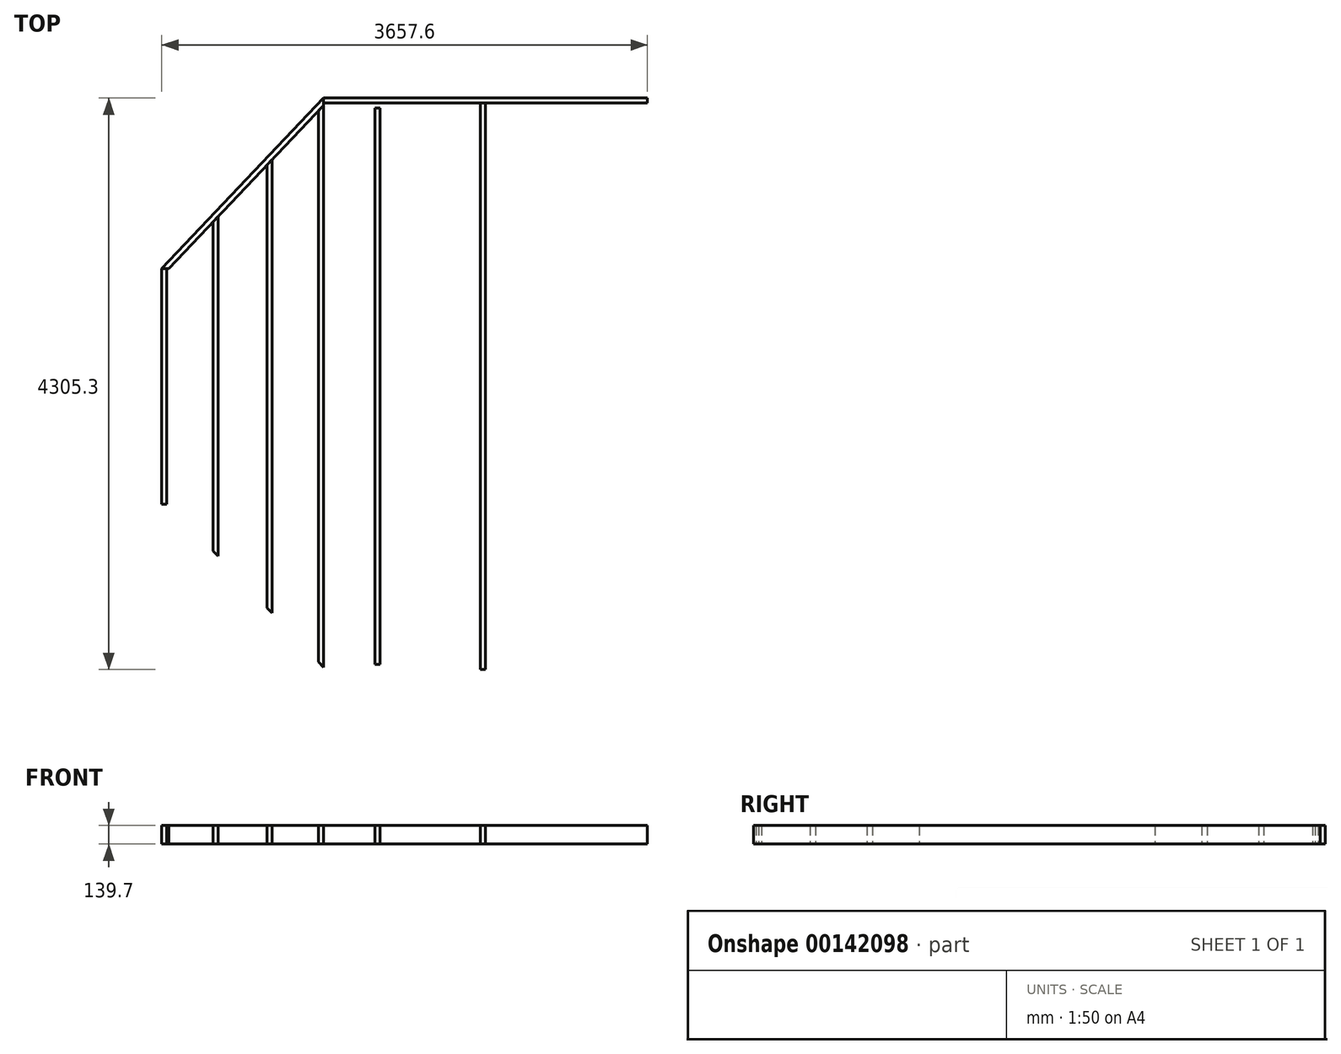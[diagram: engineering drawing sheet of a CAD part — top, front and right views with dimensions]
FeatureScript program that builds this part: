
annotation { "Feature Type Name" : "Feature", "Feature Type Description" : "" }
export const myFeature = defineFeature(function(context is Context, id is Id, definition is map)
    precondition{}
    {
        {
            var Q0;
            Q0=qCreatedBy(makeId("Top.planeOp"),FACE);
            var sketch = newSketch(context, id + "F0", { "sketchPlane" : qUnion([Q0])});
            skLineSegment(sketch, "E0", {"start": v(0, 0) * mm, "end": v(19.05, 0) * mm});
            skLineSegment(sketch, "E1.bottom", {"start": v(38.1, 2133.6) * mm, "end": v(0, 2133.6) * mm});
            skLineSegment(sketch, "E1.top", {"start": v(38.1, -2133.6) * mm, "end": v(0, -2133.6) * mm});
            skLineSegment(sketch, "E1.left", {"start": v(38.1, 2133.6) * mm, "end": v(38.1, -2133.6) * mm});
            skLineSegment(sketch, "E1.right", {"start": v(0, 2133.6) * mm, "end": v(0, -2133.6) * mm});
            skPoint(sketch, "E1.middle", {"position": v(19.05, 0) * mm});
            skLineSegment(sketch, "E2.bottom", {"start": v(38.1, 2133.6) * mm, "end": v(1181.1, 2133.6) * mm});
            skLineSegment(sketch, "E2.top", {"start": v(38.1, 2095.5) * mm, "end": v(1181.1, 2095.5) * mm});
            skLineSegment(sketch, "E2.left", {"start": v(38.1, 2133.6) * mm, "end": v(38.1, 2095.5) * mm});
            skLineSegment(sketch, "E2.right", {"start": v(1181.1, 2133.6) * mm, "end": v(1181.1, 2095.5) * mm});
            skLineSegment(sketch, "E3.bottom", {"start": v(1181.1, 2133.6) * mm, "end": v(1219.2, 2133.6) * mm});
            skLineSegment(sketch, "E3.top", {"start": v(1181.1, -2133.6) * mm, "end": v(1219.2, -2133.6) * mm});
            skLineSegment(sketch, "E3.left", {"start": v(1181.1, 2133.6) * mm, "end": v(1181.1, -2133.6) * mm});
            skLineSegment(sketch, "E3.right", {"start": v(1219.2, 2133.6) * mm, "end": v(1219.2, -2133.6) * mm});
            skLineSegment(sketch, "E4.MirrorCS", {"start": v(38.1, -2095.5) * mm, "end": v(1181.1, -2095.5) * mm});
            skLineSegment(sketch, "E5.MirrorCS", {"start": v(38.1, -2133.6) * mm, "end": v(1181.1, -2133.6) * mm});
            skLineSegment(sketch, "E6.bottom", {"start": v(387.35, 2095.5) * mm, "end": v(425.45, 2095.5) * mm});
            skLineSegment(sketch, "E6.top", {"start": v(387.35, -2095.5) * mm, "end": v(425.45, -2095.5) * mm});
            skLineSegment(sketch, "E6.left", {"start": v(387.35, 2095.5) * mm, "end": v(387.35, -2095.5) * mm});
            skLineSegment(sketch, "E6.right", {"start": v(425.45, 2095.5) * mm, "end": v(425.45, -2095.5) * mm});
            skLineSegment(sketch, "E7.bottom", {"start": v(793.75, 2095.5) * mm, "end": v(831.85, 2095.5) * mm});
            skLineSegment(sketch, "E7.top", {"start": v(793.75, -2095.5) * mm, "end": v(831.85, -2095.5) * mm});
            skLineSegment(sketch, "E7.left", {"start": v(793.75, 2095.5) * mm, "end": v(793.75, -2095.5) * mm});
            skLineSegment(sketch, "E7.right", {"start": v(831.85, 2095.5) * mm, "end": v(831.85, -2095.5) * mm});
            skLineSegment(sketch, "E8.bottom", {"start": v(1219.2, -2133.6) * mm, "end": v(-1219.2, -2133.6) * mm});
            skLineSegment(sketch, "E8.top", {"start": v(1219.2, -2171.7) * mm, "end": v(-1219.2, -2171.7) * mm});
            skLineSegment(sketch, "E8.left", {"start": v(1219.2, -2133.6) * mm, "end": v(1219.2, -2171.7) * mm});
            skLineSegment(sketch, "E8.right", {"start": v(-1219.2, -2133.6) * mm, "end": v(-1219.2, -2171.7) * mm});
            skLineSegment(sketch, "E9.MirrorCS", {"start": v(1219.2, 2133.6) * mm, "end": v(-1219.2, 2133.6) * mm});
            skLineSegment(sketch, "E10.MirrorCS", {"start": v(1219.2, 2171.7) * mm, "end": v(-1219.2, 2171.7) * mm});
            skLineSegment(sketch, "E11.MirrorCS", {"start": v(1219.2, 2133.6) * mm, "end": v(1219.2, 2171.7) * mm});
            skLineSegment(sketch, "E12.MirrorCS", {"start": v(-1219.2, 2133.6) * mm, "end": v(-1219.2, 2171.7) * mm});
            skLineSegment(sketch, "E13", {"start": v(1219.2, -2171.7) * mm, "end": v(2438.4, -886.93) * mm});
            skLineSegment(sketch, "E14", {"start": v(2438.4, -886.93) * mm, "end": v(2438.4, 886.93) * mm});
            skLineSegment(sketch, "E15", {"start": v(2438.4, 886.93) * mm, "end": v(1219.2, 2171.7) * mm});
            skLineSegment(sketch, "E16", {"start": v(1219.2, 2116.35) * mm, "end": v(2385.88, 886.93) * mm});
            skLineSegment(sketch, "E17", {"start": v(2385.88, 886.93) * mm, "end": v(2438.4, 886.93) * mm});
            skLineSegment(sketch, "E18.MirrorCS", {"start": v(1219.2, -2116.35) * mm, "end": v(2385.88, -886.93) * mm});
            skLineSegment(sketch, "E19.MirrorCS", {"start": v(2385.88, -886.93) * mm, "end": v(2438.4, -886.93) * mm});
            skLineSegment(sketch, "E20.bottom", {"start": v(2438.4, -886.93) * mm, "end": v(2400.3, -886.93) * mm});
            skLineSegment(sketch, "E20.top", {"start": v(2438.4, 886.93) * mm, "end": v(2400.3, 886.93) * mm});
            skLineSegment(sketch, "E20.right", {"start": v(2400.3, -886.93) * mm, "end": v(2400.3, 886.93) * mm});
            skLineSegment(sketch, "E21", {"start": v(2051.05, 1239.76) * mm, "end": v(2051.05, -1239.76) * mm});
            skLineSegment(sketch, "E22", {"start": v(2012.95, 1279.91) * mm, "end": v(2012.95, -1279.91) * mm});
            skLineSegment(sketch, "E23", {"start": v(1644.65, 1668.02) * mm, "end": v(1644.65, -1668.02) * mm});
            skLineSegment(sketch, "E24", {"start": v(1606.55, -1708.17) * mm, "end": v(1606.55, 1708.17) * mm});
            skLineSegment(sketch, "E25", {"start": v(1257.3, 2076.2) * mm, "end": v(1257.3, -2076.2) * mm});
            skLineSegment(sketch, "E26.MirrorCS", {"start": v(-2438.4, -886.93) * mm, "end": v(-2438.4, 886.93) * mm});
            skLineSegment(sketch, "E27.MirrorCS", {"start": v(-1257.3, 2076.2) * mm, "end": v(-1257.3, -2076.2) * mm});
            skLineSegment(sketch, "E28.MirrorCS", {"start": v(-2051.05, 1239.76) * mm, "end": v(-2051.05, -1239.76) * mm});
            skLineSegment(sketch, "E29.MirrorCS", {"start": v(-831.85, 2095.5) * mm, "end": v(-831.85, -2095.5) * mm});
            skLineSegment(sketch, "E30.MirrorCS", {"start": v(-793.75, 2095.5) * mm, "end": v(-793.75, -2095.5) * mm});
            skLineSegment(sketch, "E31.MirrorCS", {"start": v(-1644.65, 1668.02) * mm, "end": v(-1644.65, -1668.02) * mm});
            skLineSegment(sketch, "E32.MirrorCS", {"start": v(-1606.55, -1708.17) * mm, "end": v(-1606.55, 1708.17) * mm});
            skLineSegment(sketch, "E33.MirrorCS", {"start": v(-425.45, 2095.5) * mm, "end": v(-425.45, -2095.5) * mm});
            skLineSegment(sketch, "E34.MirrorCS", {"start": v(-387.35, 2095.5) * mm, "end": v(-387.35, -2095.5) * mm});
            skLineSegment(sketch, "E35.MirrorCS", {"start": v(-2400.3, -886.93) * mm, "end": v(-2400.3, 886.93) * mm});
            skLineSegment(sketch, "E36.MirrorCS", {"start": v(-1219.2, 2133.6) * mm, "end": v(-1219.2, -2133.6) * mm});
            skLineSegment(sketch, "E37.MirrorCS", {"start": v(-1181.1, 2133.6) * mm, "end": v(-1181.1, -2133.6) * mm});
            skLineSegment(sketch, "E38.MirrorCS", {"start": v(-2012.95, 1279.91) * mm, "end": v(-2012.95, -1279.91) * mm});
            skLineSegment(sketch, "E39.MirrorCS", {"start": v(-1219.2, 2116.35) * mm, "end": v(-2385.88, 886.93) * mm});
            skLineSegment(sketch, "E40.MirrorCS", {"start": v(-2438.4, 886.93) * mm, "end": v(-1219.2, 2171.7) * mm});
            skLineSegment(sketch, "E41.MirrorCS", {"start": v(-2385.88, 886.93) * mm, "end": v(-2438.4, 886.93) * mm});
            skLineSegment(sketch, "E42.MirrorCS", {"start": v(-2438.4, 886.93) * mm, "end": v(-2400.3, 886.93) * mm});
            skLineSegment(sketch, "E43.MirrorCS", {"start": v(-1181.1, -2133.6) * mm, "end": v(-1219.2, -2133.6) * mm});
            skLineSegment(sketch, "E44.MirrorCS", {"start": v(-38.1, -2133.6) * mm, "end": v(-1181.1, -2133.6) * mm});
            skLineSegment(sketch, "E45.MirrorCS", {"start": v(-1219.2, -2171.7) * mm, "end": v(-2438.4, -886.93) * mm});
            skLineSegment(sketch, "E46.MirrorCS", {"start": v(-38.1, -2095.5) * mm, "end": v(-1181.1, -2095.5) * mm});
            skLineSegment(sketch, "E47.MirrorCS", {"start": v(-1219.2, -2133.6) * mm, "end": v(1219.2, -2133.6) * mm});
            skLineSegment(sketch, "E48.MirrorCS", {"start": v(-1219.2, -2171.7) * mm, "end": v(1219.2, -2171.7) * mm});
            skLineSegment(sketch, "E49.MirrorCS", {"start": v(-1219.2, -2116.35) * mm, "end": v(-2385.88, -886.93) * mm});
            skLineSegment(sketch, "E50.MirrorCS", {"start": v(-38.1, 2095.5) * mm, "end": v(-1181.1, 2095.5) * mm});
            skLineSegment(sketch, "E51.MirrorCS", {"start": v(-38.1, 2133.6) * mm, "end": v(-38.1, -2133.6) * mm});
            skLineSegment(sketch, "E52.MirrorCS", {"start": v(-2438.4, -886.93) * mm, "end": v(-2400.3, -886.93) * mm});
            skLineSegment(sketch, "E53.MirrorCS", {"start": v(-2385.88, -886.93) * mm, "end": v(-2438.4, -886.93) * mm});
            skSolve(sketch);
        }
        {
            var Q0;
            {var subQ0=sQuery(id+"F0.wireOp",EDGE,"E26.MirrorCS");Q0=makeQuery(id+"F0.imprint","IMPRINT",FACE,{"disambiguationData":[TD([[makeQuery(id+"F0.imprint","IMPRINT",EDGE,{"derivedFrom":subQ0}),-1.0]])]});}
            var Q1;
            {var subQ0=sQuery(id+"F0.wireOp",EDGE,"E28.MirrorCS");Q1=makeQuery(id+"F0.imprint","IMPRINT",FACE,{"disambiguationData":[TD([[makeQuery(id+"F0.imprint","IMPRINT",EDGE,{"derivedFrom":subQ0}),1.0]])]});}
            var Q2;
            {var subQ0=sQuery(id+"F0.wireOp",EDGE,"E31.MirrorCS");Q2=makeQuery(id+"F0.imprint","IMPRINT",FACE,{"disambiguationData":[TD([[makeQuery(id+"F0.imprint","IMPRINT",EDGE,{"derivedFrom":subQ0}),1.0]])]});}
            var Q3;
            {var subQ3=sQuery(id+"F0.wireOp",EDGE,"E27.MirrorCS");Q3=makeQuery(id+"F0.imprint","IMPRINT",FACE,{"disambiguationData":[TD([[makeQuery(id+"F0.imprint","IMPRINT",EDGE,{"derivedFrom":subQ3}),1.0]])]});}
            var Q4;
            {var subQ0=sQuery(id+"F0.wireOp",EDGE,"E29.MirrorCS");Q4=makeQuery(id+"F0.imprint","IMPRINT",FACE,{"disambiguationData":[TD([[makeQuery(id+"F0.imprint","IMPRINT",EDGE,{"derivedFrom":subQ0}),1.0]])]});}
            var Q5;
            {var subQ1=sQuery(id+"F0.wireOp",EDGE,"E1.right");var subQ10=makeQuery(id+"F0.imprint","IMPRINT",VERTEX,{"derivedFrom":subQ1});Q5=makeQuery(id+"F0.imprint","IMPRINT",FACE,{"disambiguationData":[TD([[makeQuery(id+"F0.imprint","IMPRINT",EDGE,{"disambiguationData":[TD([[subQ10,1.0]])],"derivedFrom":subQ1}),-1.0]])]});}
            var Q6;
            {var subQ0=sQuery(id+"F0.wireOp",EDGE,"E6.top");Q6=makeQuery(id+"F0.imprint","IMPRINT",FACE,{"disambiguationData":[TD([[makeQuery(id+"F0.imprint","IMPRINT",EDGE,{"derivedFrom":subQ0}),-1.0]])]});}
            extrude(context, id + "F1", {"entities" : qUnion([Q0, Q1, Q2, Q3, Q4, Q5, Q6]), "depth" : 139.7 * mm, "symmetric" : true});
        }
        {
            var Q0;
            Q0=makeQuery(id+"F0.imprint","IMPRINT",FACE,{"disambiguationData":[TD([[makeQuery(id+"F0.imprint","IMPRINT",EDGE,{"derivedFrom":sQuery(id+"F0.wireOp",EDGE,"E10.MirrorCS")}),1.0]])]});
            extrude(context, id + "F2", {"entities" : qUnion([Q0]), "depth" : 139.7 * mm, "symmetric" : true});
        }
        {
            var Q0;
            {var subQ5=sQuery(id+"F0.wireOp",EDGE,"E12.MirrorCS");Q0=makeQuery(id+"F0.imprint","IMPRINT",FACE,{"disambiguationData":[TD([[makeQuery(id+"F0.imprint","IMPRINT",EDGE,{"derivedFrom":subQ5}),1.0]])]});}
            extrude(context, id + "F3", {"entities" : qUnion([Q0]), "depth" : 139.7 * mm, "symmetric" : true});
        }
    });
